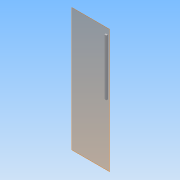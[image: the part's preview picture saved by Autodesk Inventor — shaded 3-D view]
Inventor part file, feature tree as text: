
AUTODESK INVENTOR PART (.ipt)
format: ipt  version: 2013 (Build 170138000, 138)  size: 78,848 bytes
history: native  units: in
note: dims shown in document units (in); Inventor stores cm internally (conversion verified against a paired STEP export)
features: extrude x2, sketch x2, plane x1
ambient origin geometry x8: Origin, YZ Plane, XZ Plane, XY Plane, X Axis, Y Axis, Z Axis, Center Point
bodies: Solid1 (feature_tree)
feature tree (5):
  plane  "Work Plane1"
  extrude  "Extrusion1"  Depth=1.5in
  extrude  "Extrusion2"  TaperAngle=0.0deg  [1 undecoded]
  sketch  "Sketch1"  dims[d0=39.0in d2=1.5in]
  sketch  "Sketch2"  dims[d3=1.0in d4=0.0in d5=38.5in d7=0.5in d8=0.3332in d9=0.0in]
note: 1 required parameter value undecoded (feature->parameter linkage not recoverable at this tier; creation-order binding heuristic only, values carry confidence <= 0.55)
